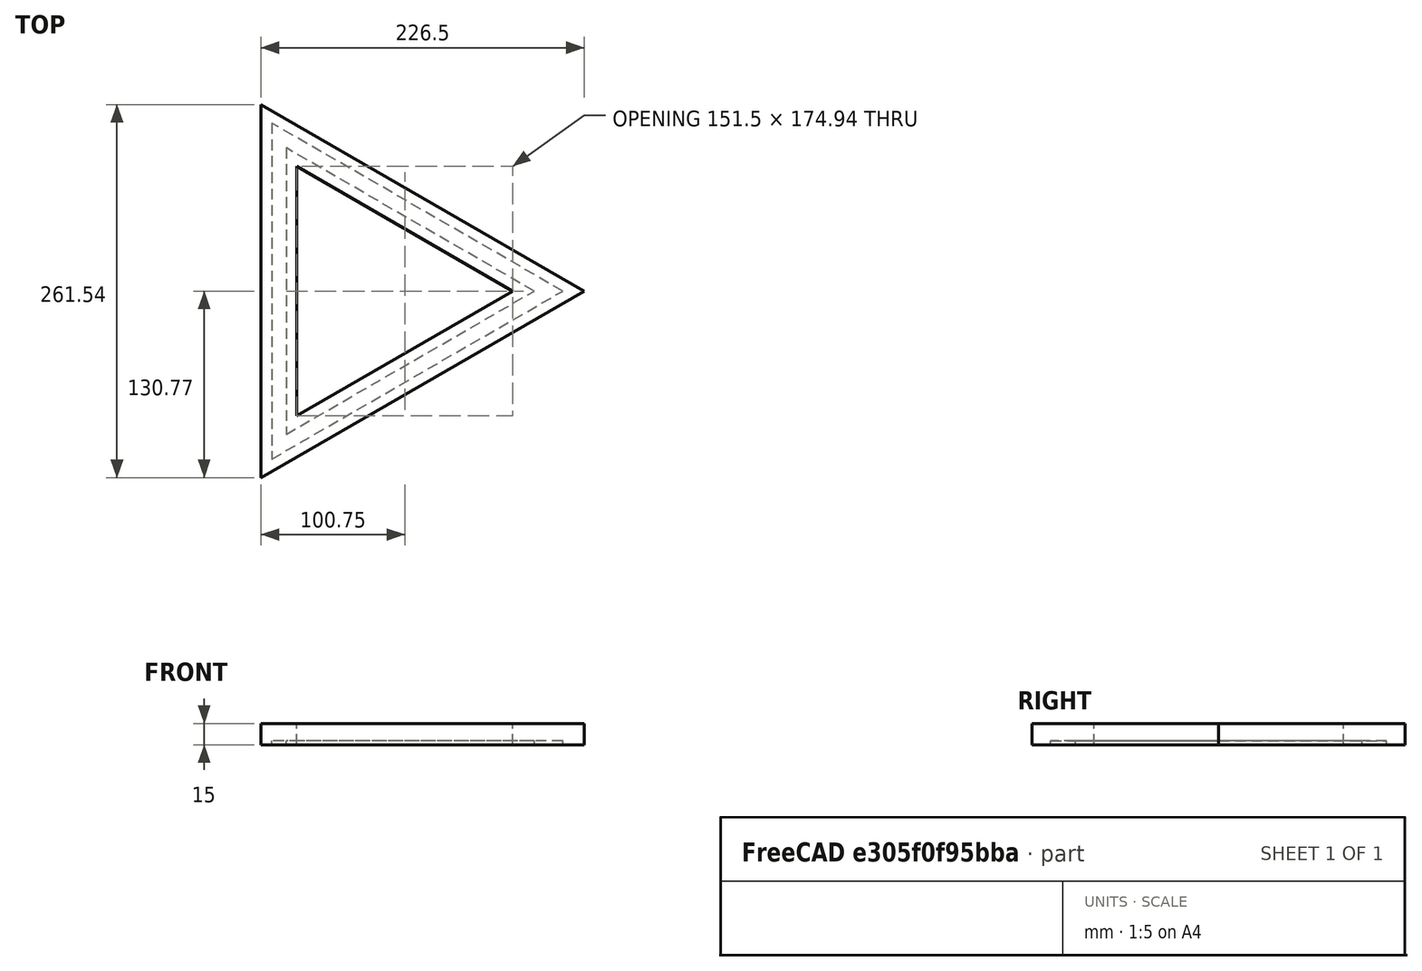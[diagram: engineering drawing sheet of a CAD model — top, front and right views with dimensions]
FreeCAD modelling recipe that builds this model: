
FCSTD DOCUMENT  (FreeCAD 0.15R4671 (Git))
Label: Triangle-Light-36-grooves
License: All rights reserved
LicenseURL: http://en.wikipedia.org/wiki/All_rights_reserved
objects: App::MeasureDistance×6, Part::Prism×4, Part::Cut×3
note: 7 computed .brp shape members not serialized (recipe doc carries the construction recipe); baked Part::Feature solids carry a one-line shape summary decoded from their .brp

FEATURE [Part::Prism] Prism
  Circumradius = 136
  Height = 3
  Polygon = 3
FEATURE [Part::Prism] Prism001
  Circumradius = 116
  Height = 3
  Polygon = 3
FEATURE [Part::Cut] Cut
  Base = -> Prism
  Tool = -> Prism001
FEATURE [Part::Prism] Prism002
  Circumradius = 151
  Height = 15
  Polygon = 3
FEATURE [Part::Prism] Prism003
  Circumradius = 101
  Height = 15
  Polygon = 3
FEATURE [Part::Cut] Cut001
  Base = -> Prism002
  Tool = -> Cut
FEATURE [Part::Cut] Cut002
  Base = -> Cut001
  Tool = -> Prism003
FEATURE [App::MeasureDistance] Distance  label="Distance: 200.918"
  Distance = 200.918
  P1 = (-58,100.459,0)
  P2 = (116,0,0)
FEATURE [App::MeasureDistance] Distance001  label="Distance: 235.559"
  Distance = 235.559
  P1 = (-68,117.779,0)
  P2 = (136,0,0)
FEATURE [App::MeasureDistance] Distance002  label="Distance: 261.540"
  Distance = 261.54
  P1 = (-75.5,130.77,0)
  P2 = (151,0,0)
FEATURE [App::MeasureDistance] Distance003  label="Distance: 174.937"
  Distance = 174.937
  P1 = (-50.5,87.4686,0)
  P2 = (101,0,0)
FEATURE [App::MeasureDistance] Distance005  label="Distance: 7.530"
  Distance = 7.53007
  P1 = (38.3562,65.0349,0)
  P2 = (34.0239,58.8759,0)
FEATURE [App::MeasureDistance] Distance006  label="Distance: 10.351"
  Distance = 10.3512
  P1 = (-68,-2.93268,0)
  P2 = (-58,-0.259196,0)
